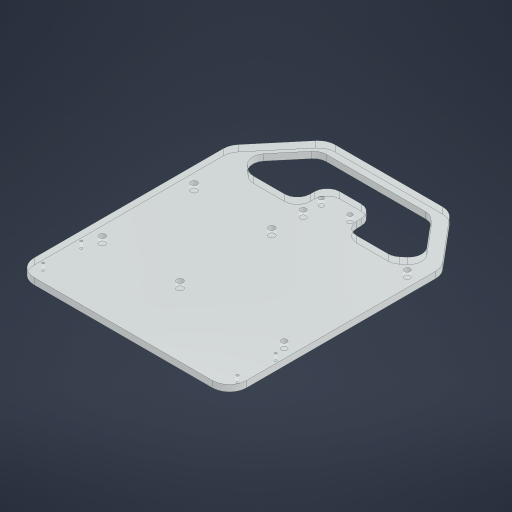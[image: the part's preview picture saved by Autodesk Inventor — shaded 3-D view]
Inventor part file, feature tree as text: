
AUTODESK INVENTOR PART (.ipt)
format: ipt  version: 2023 (Build 270158000, 158)  size: 271,872 bytes
history: native  units: mm
features: extrude x1, fillet x1, sketch x1
ambient origin geometry x8: Origin, YZ Plane, XZ Plane, XY Plane, X Axis, Y Axis, Z Axis, Center Point
bodies: Solid1 (feature_tree)
feature tree (3):
  extrude  "Extrusion1"  Depth=100.0mm
  fillet  "Fillet1"  Radius=8.0mm
  sketch  "Sketch1"  dims[d0=100.0mm d1=100.0mm d2=8.0mm d3=4.25mm d4=1.15mm d5=18.0mm d6=43.18mm d7=36.576mm d8=3.0mm d9=49.0mm d10=58.0mm d15=2.75mm d16=13.462mm d17=2.286mm d27=3.0mm d28=0.0mm d33=22.0mm d34=25.0mm d36=22.68928mm d37=6.0mm d38=6.0mm d39=14.0mm d40=6.0mm d41=8.0mm]
